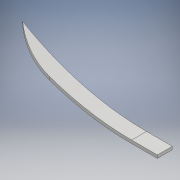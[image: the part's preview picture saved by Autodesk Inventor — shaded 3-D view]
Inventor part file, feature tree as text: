
AUTODESK INVENTOR PART (.ipt)
format: ipt  version: 2018.3 (Build 223284000, 284)  size: 152,064 bytes
history: native  units: mm
features: projected_geometry x4, other x3, extrude x3, sketch x3
ambient origin geometry x8: Origin, YZ Plane, XZ Plane, XY Plane, X Axis, Y Axis, Z Axis, Center Point
bodies: Body1 (feature_tree)
feature tree (13):
  other  "endplate_ver2.ipt"
  extrude  "押し出し1"  Depth=10.0mm
  extrude  "押し出し2"  Depth=10.0mm TaperAngle=0.0deg
  extrude  "押し出し3"  Depth=10.0mm TaperAngle=0.0deg
  other  "ソリッド2::endplate_ver2.ipt"
  other  "TaggingFeature1"
  sketch  "スケッチ1"
  projected_geometry  "投影ループ1"
  projected_geometry  "投影ループ2"
  sketch  "スケッチ2"
  projected_geometry  "投影ループ3"
  sketch  "スケッチ3"
  projected_geometry  "投影ループ4"
